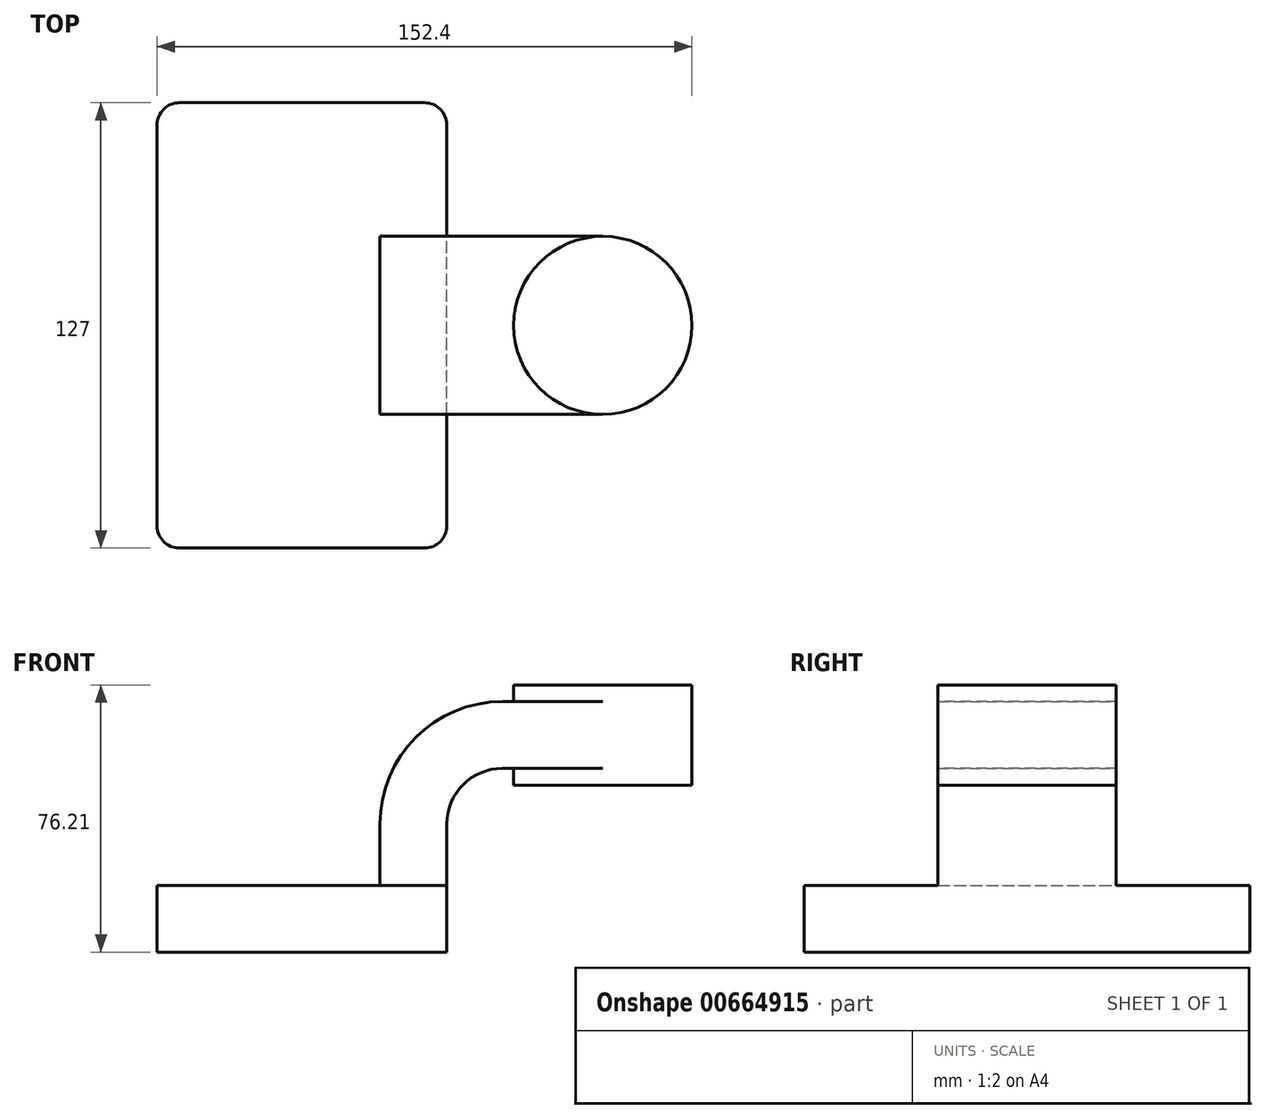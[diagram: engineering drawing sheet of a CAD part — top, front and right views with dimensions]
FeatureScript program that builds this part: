
annotation { "Feature Type Name" : "Feature", "Feature Type Description" : "" }
export const myFeature = defineFeature(function(context is Context, id is Id, definition is map)
    precondition{}
    {
        {
            var Q0;
            Q0=qCreatedBy(makeId("Front.planeOp"),FACE);
            var sketch = newSketch(context, id + "F0", { "sketchPlane" : qUnion([Q0])});
            skLineSegment(sketch, "E0.bottom", {"start": v(41.28, -9.52) * mm, "end": v(-41.28, -9.52) * mm});
            skLineSegment(sketch, "E0.top", {"start": v(41.28, 9.53) * mm, "end": v(-41.28, 9.53) * mm});
            skLineSegment(sketch, "E0.left", {"start": v(41.28, -9.52) * mm, "end": v(41.28, 9.53) * mm});
            skLineSegment(sketch, "E0.right", {"start": v(-41.28, -9.52) * mm, "end": v(-41.28, 9.53) * mm});
            skPoint(sketch, "E0.middle", {"position": v(0, 0) * mm});
            skLineSegment(sketch, "E1.bottom", {"start": v(60.33, 38.1) * mm, "end": v(111.13, 38.1) * mm});
            skLineSegment(sketch, "E1.top", {"start": v(60.32, 66.68) * mm, "end": v(111.12, 66.68) * mm});
            skLineSegment(sketch, "E1.left", {"start": v(60.33, 38.1) * mm, "end": v(60.32, 66.68) * mm});
            skLineSegment(sketch, "E1.right", {"start": v(111.13, 38.1) * mm, "end": v(111.12, 66.68) * mm});
            skPoint(sketch, "E1.middle", {"position": v(85.72, 52.39) * mm});
            skLineSegment(sketch, "E2", {"start": v(41.28, 9.53) * mm, "end": v(41.28, 27) * mm});
            skArc(sketch, "E3", {"start": v(41.27, 27) * mm, "mid": v(45.92, 38.23) * mm, "end": v(57.15, 42.88) * mm});
            skLineSegment(sketch, "E4", {"start": v(57.15, 42.88) * mm, "end": v(85.72, 42.88) * mm});
            skLineSegment(sketch, "E5", {"start": v(57.15, 42.88) * mm, "end": v(57.15, 42.88) * mm});
            skArc(sketch, "E6.0", {"start": v(22.23, 27) * mm, "mid": v(32.45, 51.7) * mm, "end": v(57.15, 61.93) * mm});
            skLineSegment(sketch, "E6.1", {"start": v(22.22, 9.53) * mm, "end": v(22.22, 27) * mm});
            skLineSegment(sketch, "E7", {"start": v(57.15, 61.93) * mm, "end": v(85.72, 61.93) * mm});
            skLineSegment(sketch, "E8", {"start": v(85.72, 61.93) * mm, "end": v(85.72, 42.88) * mm});
            skFitSpline(sketch, "E9", {"points": [v(-41.28, 9.52) * mm, v(57.15, 61.93) * mm], "startDerivative": vector(98.43, 52.4) * mm, "endDerivative": vector(128.84, 0.05) * mm});
            skLineSegment(sketch, "E10", {"start": v(85.72, 61.93) * mm, "end": v(85.73, 66.68) * mm});
            skLineSegment(sketch, "E11", {"start": v(85.72, 42.88) * mm, "end": v(85.73, 38.1) * mm});
            skSolve(sketch);
        }
        {
            var Q0;
            Q0=makeQuery(id+"F0.imprint","IMPRINT",FACE,{"disambiguationData":[TD([[makeQuery(id+"F0.imprint","IMPRINT",EDGE,{"derivedFrom":sQuery(id+"F0.wireOp",EDGE,"E0.bottom")}),-1.0]])]});
            extrude(context, id + "F1", {"entities" : qUnion([Q0]), "endBound" : BoundingType.SYMMETRIC, "depth" : 127 * mm, "offsetDistance" : 25.4 * mm});
        }
        {
            var Q0;
            {var subQ1=sQuery(id+"F0.wireOp",EDGE,"E2");Q0=makeQuery(id+"F0.imprint","IMPRINT",FACE,{"disambiguationData":[TD([[makeQuery(id+"F0.imprint","IMPRINT",EDGE,{"derivedFrom":subQ1}),1.0]])]});}
            var Q1;
            {var subQ5=sQuery(id+"F0.wireOp",EDGE,"E8");Q1=makeQuery(id+"F0.imprint","IMPRINT",FACE,{"disambiguationData":[TD([[makeQuery(id+"F0.imprint","IMPRINT",EDGE,{"derivedFrom":subQ5}),-1.0]])]});}
            extrude(context, id + "F2", {"entities" : qUnion([Q0, Q1]), "operationType" : NewBodyOperationType.ADD, "endBound" : BoundingType.SYMMETRIC, "depth" : 50.8 * mm, "offsetDistance" : 25.4 * mm});
        }
        {
            var Q0;
            Q0=makeQuery(id+"F0.imprint","IMPRINT",FACE,{"disambiguationData":[TD([[makeQuery(id+"F0.imprint","IMPRINT",EDGE,{"derivedFrom":sQuery(id+"F0.wireOp",EDGE,"E6.0")}),1.0]])]});
            extrude(context, id + "F3", {"entities" : qUnion([Q0]), "operationType" : NewBodyOperationType.ADD, "endBound" : BoundingType.SYMMETRIC, "depth" : 15.88 * mm, "offsetDistance" : 25.4 * mm});
        }
        {
            var Q0;
            {var subQ0=sQuery(id+"F0.wireOp",EDGE,"E1.right");Q0=makeQuery(id+"F0.imprint","IMPRINT",FACE,{"disambiguationData":[TD([[makeQuery(id+"F0.imprint","IMPRINT",EDGE,{"derivedFrom":subQ0}),1.0]])]});}
            var Q1;
            Q1=sQuery(id+"F0.wireOp",EDGE,"E8");
            revolve(context, id + "F4", {"operationType" : NewBodyOperationType.ADD, "entities" : qUnion([Q0]), "axis" : qUnion([Q1]), "revolveType" : RevolveType.FULL});
        }
        {
            var Q0;
            Q0=makeQuery(id+"F1.opExtrude","CAP_EDGE",EDGE,{"disambiguationData":[OSD([sQuery(id+"F0.wireOp",EDGE,"E0.left")])],"isStart":false});
            var Q1;
            Q1=makeQuery(id+"F1.opExtrude","CAP_EDGE",EDGE,{"disambiguationData":[OSD([sQuery(id+"F0.wireOp",EDGE,"E0.right")])],"isStart":false});
            var Q2;
            Q2=makeQuery(id+"F1.opExtrude","CAP_EDGE",EDGE,{"disambiguationData":[OSD([sQuery(id+"F0.wireOp",EDGE,"E0.left")])],"isStart":true});
            var Q3;
            Q3=makeQuery(id+"F1.opExtrude","CAP_EDGE",EDGE,{"disambiguationData":[OSD([sQuery(id+"F0.wireOp",EDGE,"E0.right")])],"isStart":true});
            fillet(context, id + "F5", {"entities" : qUnion([Q0, Q1, Q2, Q3]), "radius" : 6.35 * mm, "tangentPropagation" : true, "allowEdgeOverflow" : false});
        }
    });
